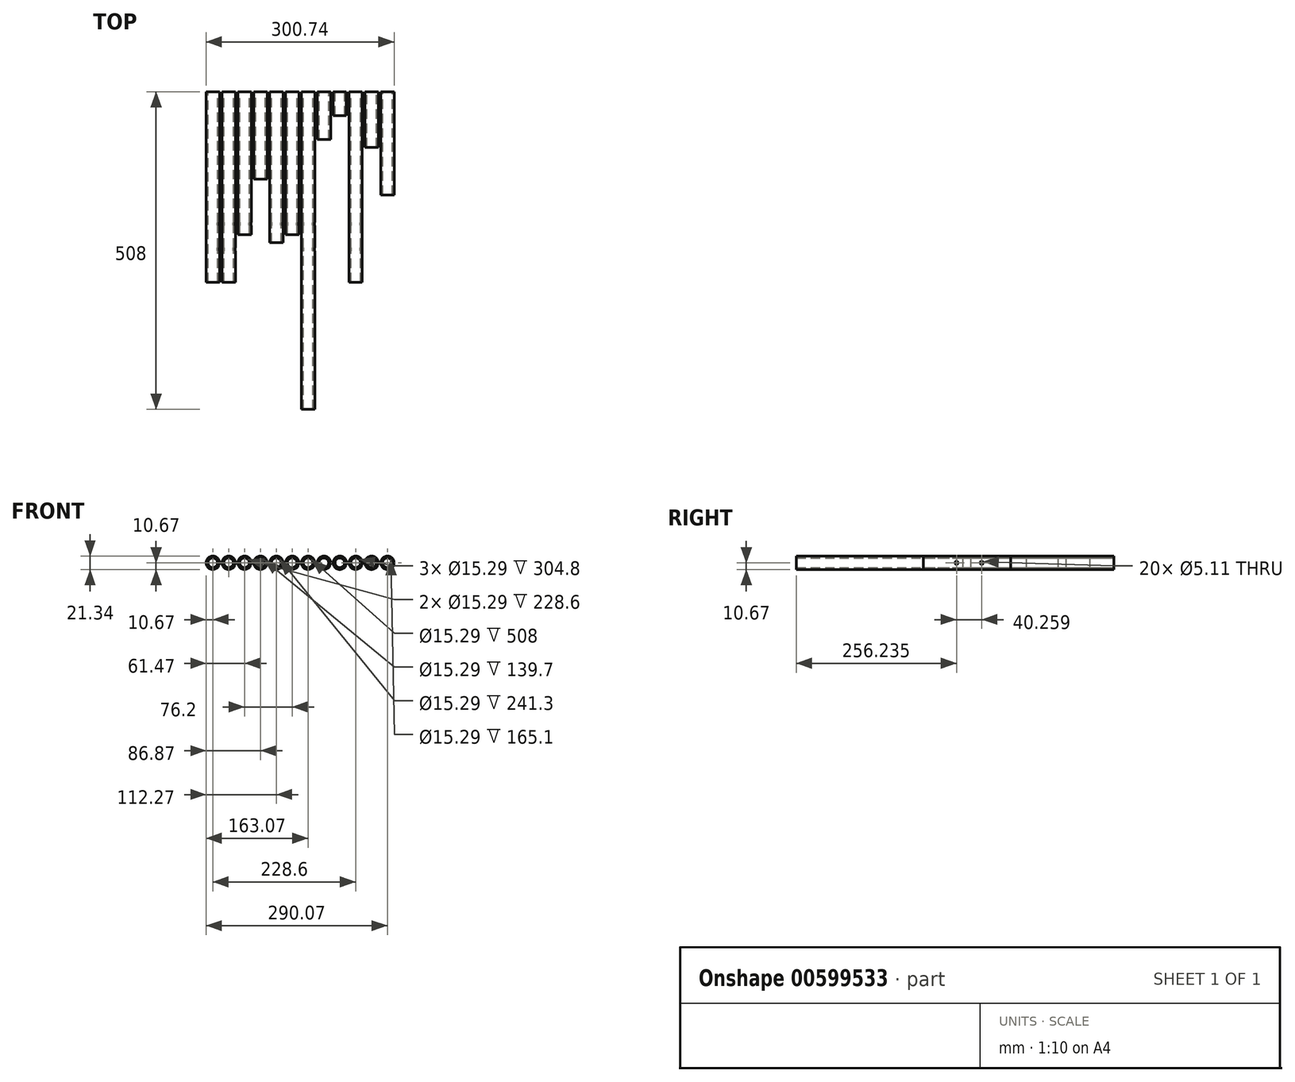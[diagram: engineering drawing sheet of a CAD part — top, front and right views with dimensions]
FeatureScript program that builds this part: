
annotation { "Feature Type Name" : "Feature", "Feature Type Description" : "" }
export const myFeature = defineFeature(function(context is Context, id is Id, definition is map)
    precondition{}
    {
        {
            var Q0;
            Q0=qCreatedBy(makeId("Front.planeOp"),FACE);
            var sketch = newSketch(context, id + "F0", { "sketchPlane" : qUnion([Q0])});
            skCircle(sketch, "E0", {"center": v(0, 0) * mm, "radius": 7.65 * mm});
            skCircle(sketch, "E1", {"center": v(0, 0) * mm, "radius": 10.67 * mm});
            skCircle(sketch, "E2.1.0.0", {"center": v(25.4, 0) * mm, "radius": 10.67 * mm});
            skCircle(sketch, "E2.1.0.1", {"center": v(25.4, 0) * mm, "radius": 7.65 * mm});
            skCircle(sketch, "E2.2.0.0", {"center": v(50.8, 0) * mm, "radius": 10.67 * mm});
            skCircle(sketch, "E2.2.0.1", {"center": v(50.8, 0) * mm, "radius": 7.65 * mm});
            skCircle(sketch, "E2.3.0.0", {"center": v(76.2, 0) * mm, "radius": 10.67 * mm});
            skCircle(sketch, "E2.3.0.1", {"center": v(76.2, 0) * mm, "radius": 7.65 * mm});
            skCircle(sketch, "E2.4.0.0", {"center": v(101.6, 0) * mm, "radius": 10.67 * mm});
            skCircle(sketch, "E2.4.0.1", {"center": v(101.6, 0) * mm, "radius": 7.65 * mm});
            skCircle(sketch, "E2.5.0.0", {"center": v(127, 0) * mm, "radius": 10.67 * mm});
            skCircle(sketch, "E2.5.0.1", {"center": v(127, 0) * mm, "radius": 7.65 * mm});
            skCircle(sketch, "E2.6.0.0", {"center": v(152.4, 0) * mm, "radius": 10.67 * mm});
            skCircle(sketch, "E2.6.0.1", {"center": v(152.4, 0) * mm, "radius": 7.65 * mm});
            skCircle(sketch, "E2.7.0.0", {"center": v(177.8, 0) * mm, "radius": 10.67 * mm});
            skCircle(sketch, "E2.7.0.1", {"center": v(177.8, 0) * mm, "radius": 7.65 * mm});
            skCircle(sketch, "E2.8.0.0", {"center": v(203.2, 0) * mm, "radius": 10.67 * mm});
            skCircle(sketch, "E2.8.0.1", {"center": v(203.2, 0) * mm, "radius": 7.65 * mm});
            skLineSegment(sketch, "E2.direction1", {"start": v(0, 0) * mm, "end": v(25.4, 0) * mm, "construction": true});
            skCircle(sketch, "E3.0.9.0", {"center": v(228.6, 0) * mm, "radius": 10.67 * mm});
            skCircle(sketch, "E3.2.9.0", {"center": v(228.6, 0) * mm, "radius": 7.65 * mm});
            skCircle(sketch, "E4.0.10.0", {"center": v(254, 0) * mm, "radius": 10.67 * mm});
            skCircle(sketch, "E4.2.10.0", {"center": v(254, 0) * mm, "radius": 7.65 * mm});
            skCircle(sketch, "E5.0.11.0", {"center": v(279.4, 0) * mm, "radius": 10.67 * mm});
            skCircle(sketch, "E5.2.11.0", {"center": v(279.4, 0) * mm, "radius": 7.65 * mm});
            skSolve(sketch);
        }
        {
            var Q0;
            Q0=makeQuery(id+"F0.imprint","IMPRINT",FACE,{"disambiguationData":[TD([[makeQuery(id+"F0.imprint","IMPRINT",EDGE,{"derivedFrom":sQuery(id+"F0.wireOp",EDGE,"E0")}),-1.0]])]});
            var Q1;
            Q1=makeQuery(id+"F0.imprint","IMPRINT",FACE,{"disambiguationData":[TD([[makeQuery(id+"F0.imprint","IMPRINT",EDGE,{"derivedFrom":sQuery(id+"F0.wireOp",EDGE,"E3.0.9.0")}),1.0]])]});
            extrude(context, id + "F1", {"entities" : qUnion([Q0, Q1]), "depth" : 304.8 * mm, "offsetDistance" : 25.4 * mm});
        }
        {
            var Q0;
            Q0=makeQuery(id+"F0.imprint","IMPRINT",FACE,{"disambiguationData":[TD([[makeQuery(id+"F0.imprint","IMPRINT",EDGE,{"derivedFrom":sQuery(id+"F0.wireOp",EDGE,"E2.1.0.0")}),1.0]])]});
            extrude(context, id + "F2", {"entities" : qUnion([Q0]), "depth" : 304.8 * mm, "offsetDistance" : 25.4 * mm});
        }
        {
            var Q0;
            Q0=makeQuery(id+"F0.imprint","IMPRINT",FACE,{"disambiguationData":[TD([[makeQuery(id+"F0.imprint","IMPRINT",EDGE,{"derivedFrom":sQuery(id+"F0.wireOp",EDGE,"E2.2.0.0")}),1.0]])]});
            extrude(context, id + "F3", {"entities" : qUnion([Q0]), "depth" : 228.6 * mm, "offsetDistance" : 25.4 * mm});
        }
        {
            var Q0;
            Q0=makeQuery(id+"F0.imprint","IMPRINT",FACE,{"disambiguationData":[TD([[makeQuery(id+"F0.imprint","IMPRINT",EDGE,{"derivedFrom":sQuery(id+"F0.wireOp",EDGE,"E2.3.0.0")}),1.0]])]});
            extrude(context, id + "F4", {"entities" : qUnion([Q0]), "depth" : 139.7 * mm, "offsetDistance" : 25.4 * mm});
        }
        {
            var Q0;
            Q0=makeQuery(id+"F0.imprint","IMPRINT",FACE,{"disambiguationData":[TD([[makeQuery(id+"F0.imprint","IMPRINT",EDGE,{"derivedFrom":sQuery(id+"F0.wireOp",EDGE,"E2.4.0.0")}),1.0]])]});
            extrude(context, id + "F5", {"entities" : qUnion([Q0]), "depth" : 241.3 * mm, "offsetDistance" : 25.4 * mm});
        }
        {
            var Q0;
            Q0=makeQuery(id+"F0.imprint","IMPRINT",FACE,{"disambiguationData":[TD([[makeQuery(id+"F0.imprint","IMPRINT",EDGE,{"derivedFrom":sQuery(id+"F0.wireOp",EDGE,"E2.5.0.0")}),1.0]])]});
            extrude(context, id + "F6", {"entities" : qUnion([Q0]), "depth" : 228.6 * mm, "offsetDistance" : 25.4 * mm});
        }
        {
            var Q0;
            Q0=makeQuery(id+"F0.imprint","IMPRINT",FACE,{"disambiguationData":[TD([[makeQuery(id+"F0.imprint","IMPRINT",EDGE,{"derivedFrom":sQuery(id+"F0.wireOp",EDGE,"E2.6.0.0")}),1.0]])]});
            extrude(context, id + "F7", {"entities" : qUnion([Q0]), "depth" : 508 * mm, "offsetDistance" : 25.4 * mm});
        }
        {
            var Q0;
            Q0=makeQuery(id+"F0.imprint","IMPRINT",FACE,{"disambiguationData":[TD([[makeQuery(id+"F0.imprint","IMPRINT",EDGE,{"derivedFrom":sQuery(id+"F0.wireOp",EDGE,"E2.7.0.0")}),1.0]])]});
            extrude(context, id + "F8", {"entities" : qUnion([Q0]), "depth" : 76.2 * mm, "offsetDistance" : 25.4 * mm});
        }
        {
            var Q0;
            Q0=makeQuery(id+"F0.imprint","IMPRINT",FACE,{"disambiguationData":[TD([[makeQuery(id+"F0.imprint","IMPRINT",EDGE,{"derivedFrom":sQuery(id+"F0.wireOp",EDGE,"E2.8.0.0")}),1.0]])]});
            extrude(context, id + "F9", {"entities" : qUnion([Q0]), "depth" : 38.1 * mm, "offsetDistance" : 25.4 * mm});
        }
        {
            var Q0;
            Q0=qCreatedBy(makeId("Right.planeOp"),FACE);
            var sketch = newSketch(context, id + "F10", { "sketchPlane" : qUnion([Q0])});
            skLineSegment(sketch, "E6.0", {"start": v(-304.8, -10.67) * mm, "end": v(-304.8, 10.67) * mm});
            skLineSegment(sketch, "E7.0", {"start": v(0, -10.67) * mm, "end": v(0, 10.67) * mm});
            skLineSegment(sketch, "E8", {"start": v(-304.8, 0) * mm, "end": v(0, 0) * mm});
            skCircle(sketch, "E9", {"center": v(-251.76, 0) * mm, "radius": 2.55 * mm});
            skCircle(sketch, "E10", {"center": v(-211.5, 0) * mm, "radius": 2.55 * mm});
            skSolve(sketch);
        }
        {
            var Q0;
            Q0 = qSketchRegion(id + "F10", true);
            extrude(context, id + "F11", {"entities" : qUnion([Q0]), "operationType" : NewBodyOperationType.REMOVE, "depth" : 304.8 * mm, "offsetDistance" : 25.4 * mm});
        }
        {
            var Q0;
            Q0=makeQuery(id+"F0.imprint","IMPRINT",FACE,{"disambiguationData":[TD([[makeQuery(id+"F0.imprint","IMPRINT",EDGE,{"derivedFrom":sQuery(id+"F0.wireOp",EDGE,"E4.0.10.0")}),1.0]])]});
            extrude(context, id + "F12", {"entities" : qUnion([Q0]), "depth" : 88.9 * mm, "offsetDistance" : 25.4 * mm});
        }
        {
            var Q0;
            Q0=makeQuery(id+"F0.imprint","IMPRINT",FACE,{"disambiguationData":[TD([[makeQuery(id+"F0.imprint","IMPRINT",EDGE,{"derivedFrom":sQuery(id+"F0.wireOp",EDGE,"E5.0.11.0")}),1.0]])]});
            extrude(context, id + "F13", {"entities" : qUnion([Q0]), "depth" : 165.1 * mm, "offsetDistance" : 25.4 * mm});
        }
    });
